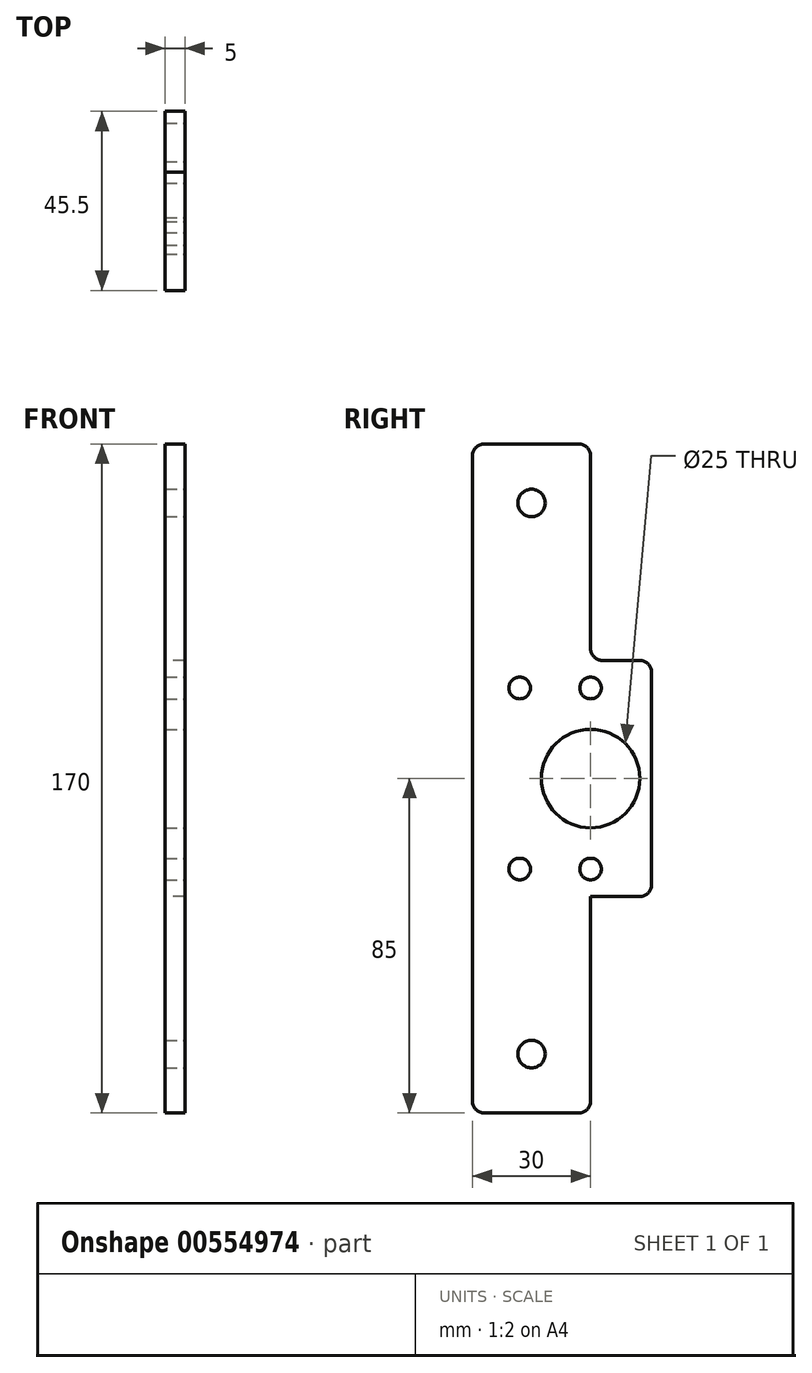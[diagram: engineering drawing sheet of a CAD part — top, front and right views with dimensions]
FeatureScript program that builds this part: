
annotation { "Feature Type Name" : "Feature", "Feature Type Description" : "" }
export const myFeature = defineFeature(function(context is Context, id is Id, definition is map)
    precondition{}
    {
        {
            var Q0;
            Q0=qCreatedBy(makeId("Right.planeOp"),FACE);
            var sketch = newSketch(context, id + "F0", { "sketchPlane" : qUnion([Q0])});
            skLineSegment(sketch, "E0.bottom", {"start": v(15, 85) * mm, "end": v(-15, 85) * mm});
            skLineSegment(sketch, "E0.top", {"start": v(15, -85) * mm, "end": v(-15, -85) * mm});
            skLineSegment(sketch, "E0.left", {"start": v(15, 85) * mm, "end": v(15, 30) * mm});
            skLineSegment(sketch, "E0.right", {"start": v(-15, 85) * mm, "end": v(-15, -85) * mm});
            skPoint(sketch, "E0.middle", {"position": v(0, 0) * mm});
            skLineSegment(sketch, "E1", {"start": v(15, 30) * mm, "end": v(30.5, 30) * mm});
            skLineSegment(sketch, "E2", {"start": v(30.5, 30) * mm, "end": v(30.5, -30) * mm});
            skLineSegment(sketch, "E3", {"start": v(30.5, -30) * mm, "end": v(15, -30) * mm});
            skLineSegment(sketch, "E4.trimOffspring", {"start": v(15, -30) * mm, "end": v(15, -85) * mm});
            skSolve(sketch);
        }
        {
            var Q0;
            Q0=qSketchRegion(id+"F0",true);
            extrude(context, id + "F1", {"entities" : qUnion([Q0]), "depth" : 5 * mm, "offsetDistance" : 25 * mm});
        }
        {
            var Q0;
            Q0=makeQuery(id+"F1.opExtrude","SWEPT_EDGE",EDGE,{"disambiguationData":[OSD([sQuery(id+"F0.wireOp",EDGE,"E0.top"),sQuery(id+"F0.wireOp",EDGE,"E0.left")])]});
            var Q1;
            Q1=makeQuery(id+"F1.opExtrude","SWEPT_EDGE",EDGE,{"disambiguationData":[OSD([sQuery(id+"F0.wireOp",EDGE,"E0.bottom"),sQuery(id+"F0.wireOp",EDGE,"E0.right")])]});
            var Q2;
            Q2=makeQuery(id+"F1.opExtrude","SWEPT_EDGE",EDGE,{"disambiguationData":[OSD([sQuery(id+"F0.wireOp",EDGE,"E0.bottom"),sQuery(id+"F0.wireOp",EDGE,"E0.left")])]});
            var Q3;
            Q3=makeQuery(id+"F1.opExtrude","SWEPT_EDGE",EDGE,{"disambiguationData":[OSD([sQuery(id+"F0.wireOp",EDGE,"E0.top"),sQuery(id+"F0.wireOp",EDGE,"E0.right")])]});
            fillet(context, id + "F2", {"entities" : qUnion([Q0, Q1, Q2, Q3]), "radius" : 3 * mm, "tangentPropagation" : true, "allowEdgeOverflow" : false});
        }
        {
            var Q0;
            Q0=makeQuery(id+"F1.opExtrude","CAP_FACE",FACE,{"disambiguationData":[OSD([sQuery(id+"F0.wireOp",EDGE,"E0.bottom"),sQuery(id+"F0.wireOp",EDGE,"E0.top"),sQuery(id+"F0.wireOp",EDGE,"E0.left"),sQuery(id+"F0.wireOp",EDGE,"E0.right")])],"isStart":false});
            var sketch = newSketch(context, id + "F3", { "sketchPlane" : qUnion([Q0])});
            skCircle(sketch, "E5", {"center": v(0, 70) * mm, "radius": 3.5 * mm});
            skCircle(sketch, "E6.MirrorC", {"center": v(0, -70) * mm, "radius": 3.5 * mm});
            skPoint(sketch, "E7.center.orphan", {"position": v(0, 40) * mm});
            skSolve(sketch);
        }
        {
            var Q0;
            Q0=qSketchRegion(id+"F3",true);
            extrude(context, id + "F4", {"entities" : qUnion([Q0]), "operationType" : NewBodyOperationType.REMOVE, "oppositeDirection" : true, "depth" : 5 * mm, "offsetDistance" : 25 * mm});
        }
        {
            var Q0;
            Q0=makeQuery(id+"F1.opExtrude","SWEPT_EDGE",EDGE,{"disambiguationData":[OSD([sQuery(id+"F0.wireOp",EDGE,"E1"),sQuery(id+"F0.wireOp",EDGE,"E2")])]});
            var Q1;
            Q1=makeQuery(id+"F1.opExtrude","SWEPT_EDGE",EDGE,{"disambiguationData":[OSD([sQuery(id+"F0.wireOp",EDGE,"E2"),sQuery(id+"F0.wireOp",EDGE,"E3")])]});
            fillet(context, id + "F5", {"entities" : qUnion([Q0, Q1]), "radius" : 3 * mm, "tangentPropagation" : true, "allowEdgeOverflow" : false});
        }
        {
            var Q0;
            Q0=makeQuery(id+"F1.opExtrude","CAP_FACE",FACE,{"disambiguationData":[OSD([sQuery(id+"F0.wireOp",EDGE,"E0.bottom"),sQuery(id+"F0.wireOp",EDGE,"E0.top"),sQuery(id+"F0.wireOp",EDGE,"E0.left"),sQuery(id+"F0.wireOp",EDGE,"E0.right"),sQuery(id+"F0.wireOp",EDGE,"E1"),sQuery(id+"F0.wireOp",EDGE,"E2"),sQuery(id+"F0.wireOp",EDGE,"E3"),sQuery(id+"F0.wireOp",EDGE,"E4.trimOffspring")])],"isStart":false});
            var sketch = newSketch(context, id + "F6", { "sketchPlane" : qUnion([Q0])});
            skCircle(sketch, "E8", {"center": v(15, 0) * mm, "radius": 12.5 * mm});
            skCircle(sketch, "E9", {"center": v(15, 23) * mm, "radius": 2.75 * mm});
            skCircle(sketch, "E10", {"center": v(15, -23) * mm, "radius": 2.75 * mm});
            skCircle(sketch, "E11", {"center": v(-3, -23) * mm, "radius": 2.75 * mm});
            skCircle(sketch, "E12", {"center": v(-3, 23) * mm, "radius": 2.75 * mm});
            skSolve(sketch);
        }
        {
            var Q0;
            Q0=qSketchRegion(id+"F6",true);
            extrude(context, id + "F7", {"entities" : qUnion([Q0]), "operationType" : NewBodyOperationType.REMOVE, "oppositeDirection" : true, "depth" : 5 * mm, "offsetDistance" : 25 * mm});
        }
    });
